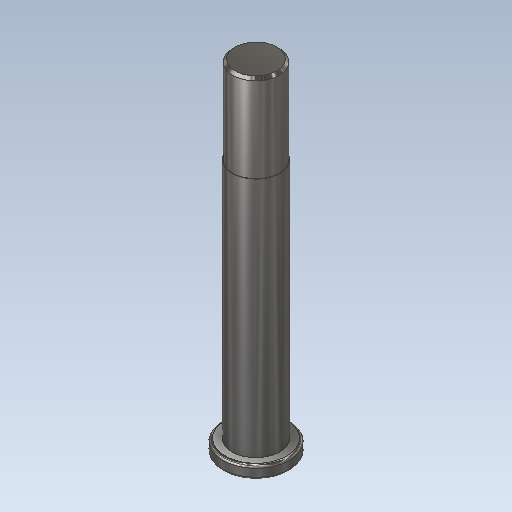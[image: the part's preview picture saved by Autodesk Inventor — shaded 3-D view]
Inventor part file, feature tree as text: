
AUTODESK INVENTOR PART (.ipt)
format: ipt  version: 2020.1 (Build 241239000, 239)  size: 124,928 bytes
history: native  units: mm
features: other x1, revolve x1, fillet x1, chamfer x1, sketch x1
ambient origin geometry x8: Origin, YZ Plane, XZ Plane, XY Plane, X Axis, Y Axis, Z Axis, Center Point
bodies: Body1 (feature_tree)
feature tree (5):
  other  "Твердое тело1"
  revolve  "Вращение1"
  fillet  "Сопряжение1"  Radius=64.0mm
  chamfer  "Фаска1"  Distance=9.3mm
  sketch  "Эскиз1"
